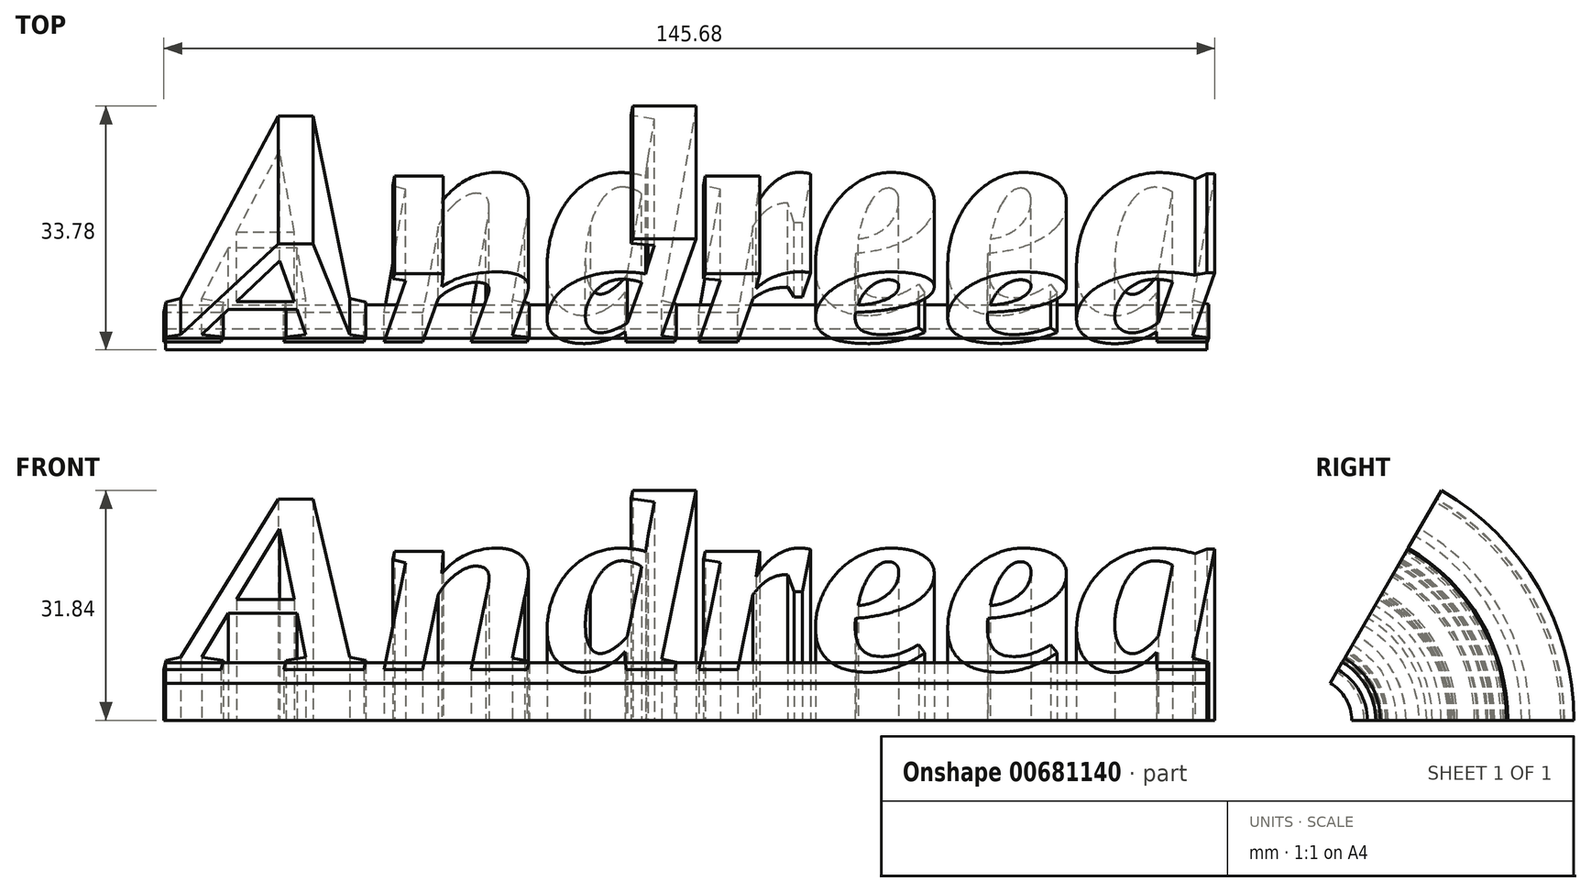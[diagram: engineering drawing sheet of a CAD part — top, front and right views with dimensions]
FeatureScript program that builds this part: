
annotation { "Feature Type Name" : "Feature", "Feature Type Description" : "" }
export const myFeature = defineFeature(function(context is Context, id is Id, definition is map)
    precondition{}
    {
        {
            var Q0;
            Q0=qCreatedBy(makeId("Top.planeOp"),FACE);
            var sketch = newSketch(context, id + "F0", { "sketchPlane" : qUnion([Q0])});
            skText(sketch, "E0", { "text": "Andreea", "fontName": "Tinos-BoldItalic.ttf"});
            const initialGuessF0  = {"E0": [-0.07616, -0.01453, 1, 0, 0.02973]};
            skSetInitialGuess(sketch, initialGuessF0);
            skSolve(sketch);
        }
        {
            var Q0;
            Q0=qCreatedBy(makeId("Top.planeOp"),FACE);
            var sketch = newSketch(context, id + "F1", { "sketchPlane" : qUnion([Q0])});
            skLineSegment(sketch, "E1.bottom", {"start": v(-78.05, -13.45) * mm, "end": v(66.3, -13.45) * mm});
            skLineSegment(sketch, "E1.top", {"start": v(-78.05, -16.7) * mm, "end": v(66.3, -16.7) * mm});
            skLineSegment(sketch, "E1.left", {"start": v(-78.05, -13.45) * mm, "end": v(-78.05, -16.7) * mm});
            skLineSegment(sketch, "E1.right", {"start": v(66.3, -13.45) * mm, "end": v(66.3, -16.7) * mm});
            skSolve(sketch);
        }
        {
            var Q0;
            Q0=qCreatedBy(makeId("Top.planeOp"),FACE);
            var sketch = newSketch(context, id + "F2", { "sketchPlane" : qUnion([Q0])});
            skLineSegment(sketch, "E2", {"start": v(-83.46, -22.64) * mm, "end": v(88.46, -22.64) * mm});
            skSolve(sketch);
        }
        {
            var Q0;
            Q0 = qSketchRegion(id + "F0", true);
            var Q1;
            Q1=makeQuery(id+"F1.imprint","IMPRINT",FACE,{"disambiguationData":[TD([[makeQuery(id+"F1.imprint","IMPRINT",EDGE,{"derivedFrom":sQuery(id+"F1.wireOp",EDGE,"E1.bottom")}),-1.0]])]});
            var Q2;
            Q2=sQuery(id+"F2.wireOp",EDGE,"E2");
            revolve(context, id + "F3", {"entities" : qUnion([Q0, Q1]), "axis" : qUnion([Q2]), "revolveType" : RevolveType.ONE_DIRECTION, "angle" : 60 * degree});
        }
    });
